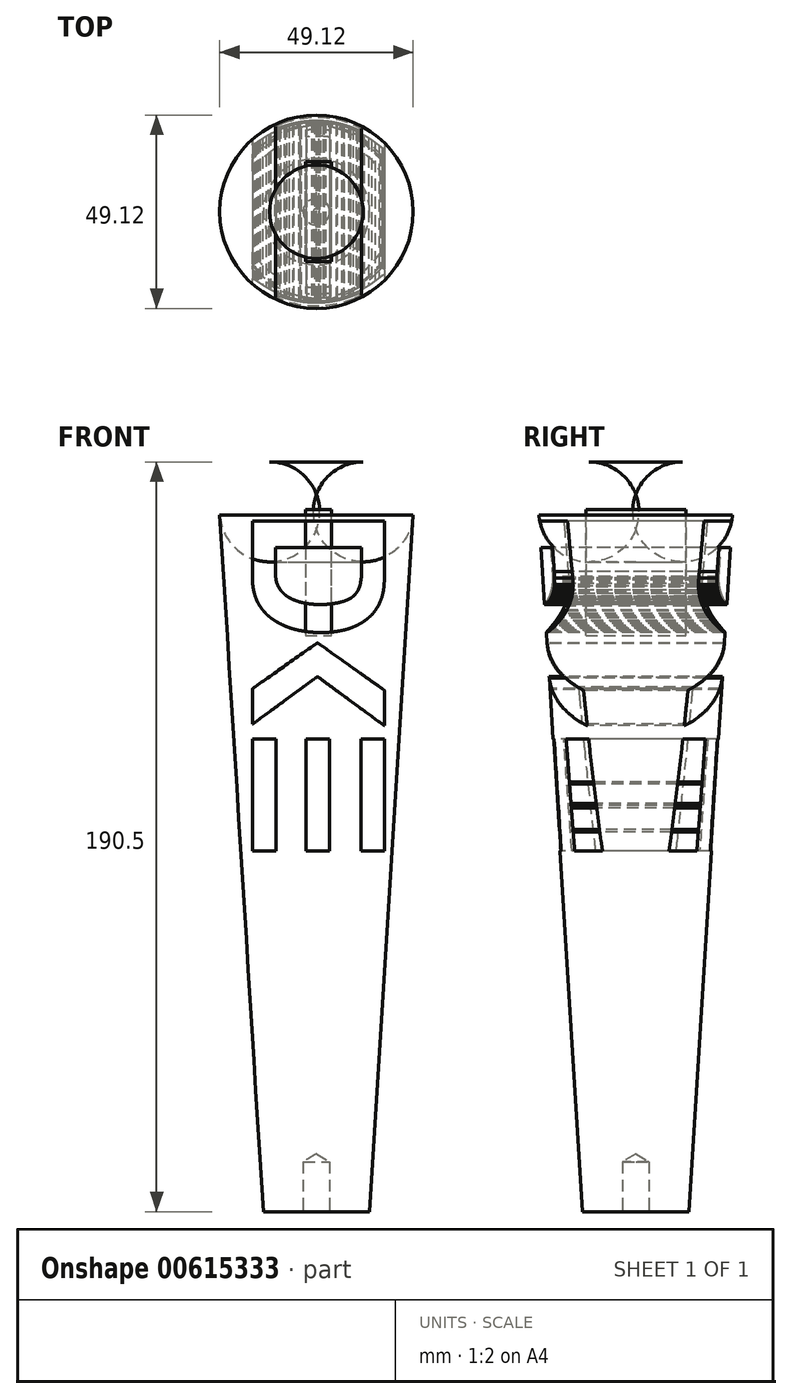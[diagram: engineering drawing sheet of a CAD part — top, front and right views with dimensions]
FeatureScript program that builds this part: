
annotation { "Feature Type Name" : "Feature", "Feature Type Description" : "" }
export const myFeature = defineFeature(function(context is Context, id is Id, definition is map)
    precondition{}
    {
        {
            var Q0;
            Q0=qCreatedBy(makeId("Front.planeOp"),FACE);
            var sketch = newSketch(context, id + "F0", { "sketchPlane" : qUnion([Q0])});
            skLineSegment(sketch, "E0", {"start": v(0, 0) * mm, "end": v(12.7, 0) * mm});
            skLineSegment(sketch, "E1", {"start": v(12.7, 0) * mm, "end": v(25.4, 203.2) * mm});
            skLineSegment(sketch, "E2", {"start": v(25.4, 203.2) * mm, "end": v(0, 203.2) * mm});
            skLineSegment(sketch, "E3", {"start": v(0, 203.2) * mm, "end": v(0, 0) * mm});
            skSolve(sketch);
        }
        {
            var Q0;
            Q0 = qSketchRegion(id + "F0", true);
            var Q1;
            Q1=sQuery(id+"F0.wireOp",EDGE,"E3");
            revolve(context, id + "F1", {"entities" : qUnion([Q0]), "axis" : qUnion([Q1]), "revolveType" : RevolveType.FULL});
        }
        {
            var Q0;
            Q0=makeQuery(id+"F1.opRevolve","SWEPT_EDGE",EDGE,{"disambiguationData":[OSD([sQuery(id+"F0.wireOp",EDGE,"E1"),sQuery(id+"F0.wireOp",EDGE,"E2")])]});
            fillet(context, id + "F2", {"entities" : qUnion([Q0]), "radius" : 12.7 * mm, "tangentPropagation" : true, "allowEdgeOverflow" : false});
        }
        {
            var Q0;
            Q0=qCreatedBy(makeId("Front.planeOp"),FACE);
            var sketch = newSketch(context, id + "F3", { "sketchPlane" : qUnion([Q0])});
            skLineSegment(sketch, "E4", {"start": v(17.27, 188.2) * mm, "end": v(17.27, 186.96) * mm});
            skLineSegment(sketch, "E5", {"start": v(17.27, 186.96) * mm, "end": v(17.27, 174.62) * mm});
            skLineSegment(sketch, "E6", {"start": v(17.27, 174.62) * mm, "end": v(17.27, 173.38) * mm});
            skLineSegment(sketch, "E7", {"start": v(17.27, 173.38) * mm, "end": v(17.26, 173.23) * mm});
            skLineSegment(sketch, "E8", {"start": v(17.26, 173.23) * mm, "end": v(17.17, 171.7) * mm});
            skLineSegment(sketch, "E9", {"start": v(17.17, 171.7) * mm, "end": v(17.16, 171.54) * mm});
            skLineSegment(sketch, "E10", {"start": v(17.16, 171.54) * mm, "end": v(17.14, 171.46) * mm});
            skLineSegment(sketch, "E11", {"start": v(17.14, 171.46) * mm, "end": v(17.04, 170.67) * mm});
            skLineSegment(sketch, "E12", {"start": v(17.04, 170.67) * mm, "end": v(17.02, 170.6) * mm});
            skLineSegment(sketch, "E13", {"start": v(17.02, 170.6) * mm, "end": v(16.96, 170.12) * mm});
            skLineSegment(sketch, "E14", {"start": v(16.96, 170.12) * mm, "end": v(16.6, 168.72) * mm});
            skLineSegment(sketch, "E15", {"start": v(16.6, 168.72) * mm, "end": v(15.88, 166.95) * mm});
            skLineSegment(sketch, "E16", {"start": v(15.88, 166.95) * mm, "end": v(14.87, 165.32) * mm});
            skLineSegment(sketch, "E17", {"start": v(14.87, 165.32) * mm, "end": v(13.94, 164.22) * mm});
            skLineSegment(sketch, "E18", {"start": v(13.94, 164.22) * mm, "end": v(13.59, 163.9) * mm});
            skLineSegment(sketch, "E19", {"start": v(13.59, 163.9) * mm, "end": v(13.22, 163.56) * mm});
            skLineSegment(sketch, "E20", {"start": v(13.22, 163.56) * mm, "end": v(12.03, 162.66) * mm});
            skLineSegment(sketch, "E21", {"start": v(12.03, 162.66) * mm, "end": v(10.3, 161.66) * mm});
            skLineSegment(sketch, "E22", {"start": v(10.3, 161.66) * mm, "end": v(8.47, 160.9) * mm});
            skLineSegment(sketch, "E23", {"start": v(8.47, 160.9) * mm, "end": v(7.04, 160.48) * mm});
            skLineSegment(sketch, "E24", {"start": v(7.04, 160.48) * mm, "end": v(6.55, 160.39) * mm});
            skLineSegment(sketch, "E25", {"start": v(6.55, 160.39) * mm, "end": v(6.42, 160.36) * mm});
            skLineSegment(sketch, "E26", {"start": v(6.42, 160.36) * mm, "end": v(5.1, 160.12) * mm});
            skLineSegment(sketch, "E27", {"start": v(5.1, 160.12) * mm, "end": v(4.96, 160.1) * mm});
            skLineSegment(sketch, "E28", {"start": v(4.96, 160.1) * mm, "end": v(4.68, 160.06) * mm});
            skLineSegment(sketch, "E29", {"start": v(4.68, 160.06) * mm, "end": v(3.29, 159.9) * mm});
            skLineSegment(sketch, "E30", {"start": v(3.29, 159.9) * mm, "end": v(1.89, 159.83) * mm});
            skLineSegment(sketch, "E31", {"start": v(1.89, 159.83) * mm, "end": v(1.6, 159.83) * mm});
            skLineSegment(sketch, "E32", {"start": v(1.6, 159.83) * mm, "end": v(1.09, 159.82) * mm});
            skLineSegment(sketch, "E33", {"start": v(1.09, 159.82) * mm, "end": v(-0.47, 159.87) * mm});
            skLineSegment(sketch, "E34", {"start": v(-0.47, 159.87) * mm, "end": v(-2.55, 160.06) * mm});
            skLineSegment(sketch, "E35", {"start": v(-2.55, 160.06) * mm, "end": v(-4.6, 160.43) * mm});
            skLineSegment(sketch, "E36", {"start": v(-4.6, 160.43) * mm, "end": v(-6.11, 160.82) * mm});
            skLineSegment(sketch, "E37", {"start": v(-6.11, 160.82) * mm, "end": v(-6.6, 160.98) * mm});
            skLineSegment(sketch, "E38", {"start": v(-6.6, 160.98) * mm, "end": v(-6.96, 161.1) * mm});
            skLineSegment(sketch, "E39", {"start": v(-6.96, 161.1) * mm, "end": v(-8.03, 161.52) * mm});
            skLineSegment(sketch, "E40", {"start": v(-8.03, 161.52) * mm, "end": v(-9.4, 162.16) * mm});
            skLineSegment(sketch, "E41", {"start": v(-9.4, 162.16) * mm, "end": v(-10.71, 162.93) * mm});
            skLineSegment(sketch, "E42", {"start": v(-10.71, 162.93) * mm, "end": v(-11.65, 163.6) * mm});
            skLineSegment(sketch, "E43", {"start": v(-11.65, 163.6) * mm, "end": v(-11.94, 163.83) * mm});
            skLineSegment(sketch, "E44", {"start": v(-11.94, 163.83) * mm, "end": v(-12.18, 164.03) * mm});
            skLineSegment(sketch, "E45", {"start": v(-12.18, 164.03) * mm, "end": v(-12.85, 164.66) * mm});
            skLineSegment(sketch, "E46", {"start": v(-12.85, 164.66) * mm, "end": v(-13.67, 165.59) * mm});
            skLineSegment(sketch, "E47", {"start": v(-13.67, 165.59) * mm, "end": v(-14.4, 166.6) * mm});
            skLineSegment(sketch, "E48", {"start": v(-14.4, 166.6) * mm, "end": v(-14.86, 167.4) * mm});
            skLineSegment(sketch, "E49", {"start": v(-14.86, 167.4) * mm, "end": v(-15, 167.67) * mm});
            skLineSegment(sketch, "E50", {"start": v(-15, 167.67) * mm, "end": v(-15.17, 168.03) * mm});
            skLineSegment(sketch, "E51", {"start": v(-15.17, 168.03) * mm, "end": v(-15.59, 169.14) * mm});
            skLineSegment(sketch, "E52", {"start": v(-15.59, 169.14) * mm, "end": v(-15.99, 170.67) * mm});
            skLineSegment(sketch, "E53", {"start": v(-15.99, 170.67) * mm, "end": v(-16.21, 172.23) * mm});
            skLineSegment(sketch, "E54", {"start": v(-16.21, 172.23) * mm, "end": v(-16.27, 173.42) * mm});
            skLineSegment(sketch, "E55", {"start": v(-16.27, 173.42) * mm, "end": v(-16.26, 173.81) * mm});
            skLineSegment(sketch, "E56", {"start": v(-16.26, 173.81) * mm, "end": v(-16.26, 175.01) * mm});
            skLineSegment(sketch, "E57", {"start": v(-16.26, 175.01) * mm, "end": v(-16.26, 187) * mm});
            skLineSegment(sketch, "E58", {"start": v(-16.26, 187) * mm, "end": v(-16.26, 188.2) * mm});
            skLineSegment(sketch, "E59", {"start": v(-16.26, 188.2) * mm, "end": v(-13.47, 188.2) * mm});
            skLineSegment(sketch, "E60", {"start": v(-13.47, 188.2) * mm, "end": v(14.47, 188.2) * mm});
            skLineSegment(sketch, "E61", {"start": v(14.47, 188.2) * mm, "end": v(17.27, 188.2) * mm});
            skLineSegment(sketch, "E62", {"start": v(16.1, 146) * mm, "end": v(16.19, 145.93) * mm});
            skLineSegment(sketch, "E63", {"start": v(16.19, 145.93) * mm, "end": v(16.69, 145.6) * mm});
            skLineSegment(sketch, "E64", {"start": v(16.69, 145.6) * mm, "end": v(17.17, 145.23) * mm});
            skLineSegment(sketch, "E65", {"start": v(17.17, 145.23) * mm, "end": v(17.26, 145.14) * mm});
            skLineSegment(sketch, "E66", {"start": v(17.26, 145.14) * mm, "end": v(17.26, 144.4) * mm});
            skLineSegment(sketch, "E67", {"start": v(17.26, 144.4) * mm, "end": v(17.26, 136.92) * mm});
            skLineSegment(sketch, "E68", {"start": v(17.26, 136.92) * mm, "end": v(17.26, 136.17) * mm});
            skLineSegment(sketch, "E69", {"start": v(17.26, 136.17) * mm, "end": v(16.35, 136.83) * mm});
            skLineSegment(sketch, "E70", {"start": v(16.35, 136.83) * mm, "end": v(7.27, 143.5) * mm});
            skLineSegment(sketch, "E71", {"start": v(7.27, 143.5) * mm, "end": v(6.36, 144.16) * mm});
            skLineSegment(sketch, "E72", {"start": v(6.36, 144.16) * mm, "end": v(5.86, 144.54) * mm});
            skLineSegment(sketch, "E73", {"start": v(5.86, 144.54) * mm, "end": v(0.78, 148.27) * mm});
            skLineSegment(sketch, "E74", {"start": v(0.78, 148.27) * mm, "end": v(0.28, 148.65) * mm});
            skLineSegment(sketch, "E75", {"start": v(0.28, 148.65) * mm, "end": v(-0.1, 148.38) * mm});
            skLineSegment(sketch, "E76", {"start": v(-0.1, 148.38) * mm, "end": v(-2.03, 146.99) * mm});
            skLineSegment(sketch, "E77", {"start": v(-2.03, 146.99) * mm, "end": v(-3.93, 145.58) * mm});
            skLineSegment(sketch, "E78", {"start": v(-3.93, 145.58) * mm, "end": v(-4.32, 145.3) * mm});
            skLineSegment(sketch, "E79", {"start": v(-4.32, 145.3) * mm, "end": v(-5.31, 144.57) * mm});
            skLineSegment(sketch, "E80", {"start": v(-5.31, 144.57) * mm, "end": v(-15.26, 137.27) * mm});
            skLineSegment(sketch, "E81", {"start": v(-15.26, 137.27) * mm, "end": v(-16.26, 136.54) * mm});
            skLineSegment(sketch, "E82", {"start": v(-16.26, 136.54) * mm, "end": v(-16.26, 137.3) * mm});
            skLineSegment(sketch, "E83", {"start": v(-16.26, 137.3) * mm, "end": v(-16.26, 143.5) * mm});
            skLineSegment(sketch, "E84", {"start": v(-16.26, 143.5) * mm, "end": v(-16.26, 145.57) * mm});
            skLineSegment(sketch, "E85", {"start": v(-16.26, 145.57) * mm, "end": v(-14.91, 146.53) * mm});
            skLineSegment(sketch, "E86", {"start": v(-14.91, 146.53) * mm, "end": v(-1.4, 156.06) * mm});
            skLineSegment(sketch, "E87", {"start": v(-1.4, 156.06) * mm, "end": v(-0.06, 157.02) * mm});
            skLineSegment(sketch, "E88", {"start": v(-0.06, 157.02) * mm, "end": v(-0.03, 157.04) * mm});
            skLineSegment(sketch, "E89", {"start": v(-0.03, 157.04) * mm, "end": v(0.06, 157.1) * mm});
            skLineSegment(sketch, "E90", {"start": v(0.06, 157.1) * mm, "end": v(0.18, 157.16) * mm});
            skLineSegment(sketch, "E91", {"start": v(0.18, 157.16) * mm, "end": v(0.31, 157.17) * mm});
            skLineSegment(sketch, "E92", {"start": v(0.31, 157.17) * mm, "end": v(0.4, 157.13) * mm});
            skLineSegment(sketch, "E93", {"start": v(0.4, 157.13) * mm, "end": v(0.43, 157.11) * mm});
            skLineSegment(sketch, "E94", {"start": v(0.43, 157.11) * mm, "end": v(1.27, 156.53) * mm});
            skLineSegment(sketch, "E95", {"start": v(1.27, 156.53) * mm, "end": v(9.58, 150.62) * mm});
            skLineSegment(sketch, "E96", {"start": v(9.58, 150.62) * mm, "end": v(10.4, 150.03) * mm});
            skLineSegment(sketch, "E97", {"start": v(10.4, 150.03) * mm, "end": v(10.88, 149.7) * mm});
            skLineSegment(sketch, "E98", {"start": v(10.88, 149.7) * mm, "end": v(15.62, 146.34) * mm});
            skLineSegment(sketch, "E99", {"start": v(15.62, 146.34) * mm, "end": v(16.1, 146) * mm});
            skLineSegment(sketch, "E100", {"start": v(11.34, 132.77) * mm, "end": v(11.83, 132.77) * mm});
            skLineSegment(sketch, "E101", {"start": v(11.83, 132.77) * mm, "end": v(16.77, 132.77) * mm});
            skLineSegment(sketch, "E102", {"start": v(16.77, 132.77) * mm, "end": v(17.27, 132.77) * mm});
            skLineSegment(sketch, "E103", {"start": v(17.27, 132.77) * mm, "end": v(17.27, 130.4) * mm});
            skLineSegment(sketch, "E104", {"start": v(17.27, 130.4) * mm, "end": v(17.27, 106.73) * mm});
            skLineSegment(sketch, "E105", {"start": v(17.27, 106.73) * mm, "end": v(17.27, 104.37) * mm});
            skLineSegment(sketch, "E106", {"start": v(17.27, 104.37) * mm, "end": v(16.77, 104.37) * mm});
            skLineSegment(sketch, "E107", {"start": v(16.77, 104.37) * mm, "end": v(11.83, 104.37) * mm});
            skLineSegment(sketch, "E108", {"start": v(11.83, 104.37) * mm, "end": v(11.34, 104.37) * mm});
            skLineSegment(sketch, "E109", {"start": v(11.34, 104.37) * mm, "end": v(11.34, 104.77) * mm});
            skLineSegment(sketch, "E110", {"start": v(11.34, 104.77) * mm, "end": v(11.34, 108.79) * mm});
            skLineSegment(sketch, "E111", {"start": v(11.34, 108.79) * mm, "end": v(11.34, 109.19) * mm});
            skLineSegment(sketch, "E112", {"start": v(11.34, 109.19) * mm, "end": v(11.32, 109.75) * mm});
            skLineSegment(sketch, "E113", {"start": v(11.32, 109.75) * mm, "end": v(11.33, 115.32) * mm});
            skLineSegment(sketch, "E114", {"start": v(11.33, 115.32) * mm, "end": v(11.34, 115.88) * mm});
            skLineSegment(sketch, "E115", {"start": v(11.34, 115.88) * mm, "end": v(11.33, 116.37) * mm});
            skLineSegment(sketch, "E116", {"start": v(11.33, 116.37) * mm, "end": v(11.32, 121.32) * mm});
            skLineSegment(sketch, "E117", {"start": v(11.32, 121.32) * mm, "end": v(11.34, 121.8) * mm});
            skLineSegment(sketch, "E118", {"start": v(11.34, 121.8) * mm, "end": v(11.34, 122.72) * mm});
            skLineSegment(sketch, "E119", {"start": v(11.34, 122.72) * mm, "end": v(11.34, 131.86) * mm});
            skLineSegment(sketch, "E120", {"start": v(11.34, 131.86) * mm, "end": v(11.34, 132.77) * mm});
            skLineSegment(sketch, "E121", {"start": v(11.46, 175.86) * mm, "end": v(11.46, 175.33) * mm});
            skLineSegment(sketch, "E122", {"start": v(11.46, 175.33) * mm, "end": v(11.39, 173.74) * mm});
            skLineSegment(sketch, "E123", {"start": v(11.39, 173.74) * mm, "end": v(11.1, 172) * mm});
            skLineSegment(sketch, "E124", {"start": v(11.1, 172) * mm, "end": v(11, 171.65) * mm});
            skLineSegment(sketch, "E125", {"start": v(11, 171.65) * mm, "end": v(10.93, 171.4) * mm});
            skLineSegment(sketch, "E126", {"start": v(10.93, 171.4) * mm, "end": v(10.62, 170.68) * mm});
            skLineSegment(sketch, "E127", {"start": v(10.62, 170.68) * mm, "end": v(10.06, 169.79) * mm});
            skLineSegment(sketch, "E128", {"start": v(10.06, 169.79) * mm, "end": v(9.34, 169.03) * mm});
            skLineSegment(sketch, "E129", {"start": v(9.34, 169.03) * mm, "end": v(8.7, 168.56) * mm});
            skLineSegment(sketch, "E130", {"start": v(8.7, 168.56) * mm, "end": v(8.47, 168.44) * mm});
            skLineSegment(sketch, "E131", {"start": v(8.47, 168.44) * mm, "end": v(8.1, 168.25) * mm});
            skLineSegment(sketch, "E132", {"start": v(8.1, 168.25) * mm, "end": v(6.92, 167.78) * mm});
            skLineSegment(sketch, "E133", {"start": v(6.92, 167.78) * mm, "end": v(5.28, 167.35) * mm});
            skLineSegment(sketch, "E134", {"start": v(5.28, 167.35) * mm, "end": v(3.6, 167.1) * mm});
            skLineSegment(sketch, "E135", {"start": v(3.6, 167.1) * mm, "end": v(2.35, 167) * mm});
            skLineSegment(sketch, "E136", {"start": v(2.35, 167) * mm, "end": v(1.92, 166.97) * mm});
            skLineSegment(sketch, "E137", {"start": v(1.92, 166.97) * mm, "end": v(1.7, 166.98) * mm});
            skLineSegment(sketch, "E138", {"start": v(1.7, 166.98) * mm, "end": v(0.53, 166.97) * mm});
            skLineSegment(sketch, "E139", {"start": v(0.53, 166.97) * mm, "end": v(-0.63, 167) * mm});
            skLineSegment(sketch, "E140", {"start": v(-0.63, 167) * mm, "end": v(-0.87, 167.03) * mm});
            skLineSegment(sketch, "E141", {"start": v(-0.87, 167.03) * mm, "end": v(-1.3, 167.06) * mm});
            skLineSegment(sketch, "E142", {"start": v(-1.3, 167.06) * mm, "end": v(-2.56, 167.23) * mm});
            skLineSegment(sketch, "E143", {"start": v(-2.56, 167.23) * mm, "end": v(-4.24, 167.6) * mm});
            skLineSegment(sketch, "E144", {"start": v(-4.24, 167.6) * mm, "end": v(-5.85, 168.16) * mm});
            skLineSegment(sketch, "E145", {"start": v(-5.85, 168.16) * mm, "end": v(-7, 168.74) * mm});
            skLineSegment(sketch, "E146", {"start": v(-7, 168.74) * mm, "end": v(-7.35, 168.97) * mm});
            skLineSegment(sketch, "E147", {"start": v(-7.35, 168.97) * mm, "end": v(-7.6, 169.13) * mm});
            skLineSegment(sketch, "E148", {"start": v(-7.6, 169.13) * mm, "end": v(-8.3, 169.7) * mm});
            skLineSegment(sketch, "E149", {"start": v(-8.3, 169.7) * mm, "end": v(-9.1, 170.6) * mm});
            skLineSegment(sketch, "E150", {"start": v(-9.1, 170.6) * mm, "end": v(-9.73, 171.61) * mm});
            skLineSegment(sketch, "E151", {"start": v(-9.73, 171.61) * mm, "end": v(-10.08, 172.44) * mm});
            skLineSegment(sketch, "E152", {"start": v(-10.08, 172.44) * mm, "end": v(-10.15, 172.73) * mm});
            skLineSegment(sketch, "E153", {"start": v(-10.15, 172.73) * mm, "end": v(-10.22, 172.96) * mm});
            skLineSegment(sketch, "E154", {"start": v(-10.22, 172.96) * mm, "end": v(-10.4, 174.13) * mm});
            skLineSegment(sketch, "E155", {"start": v(-10.4, 174.13) * mm, "end": v(-10.44, 175.3) * mm});
            skLineSegment(sketch, "E156", {"start": v(-10.44, 175.3) * mm, "end": v(-10.44, 175.54) * mm});
            skLineSegment(sketch, "E157", {"start": v(-10.44, 175.54) * mm, "end": v(-10.44, 176.03) * mm});
            skLineSegment(sketch, "E158", {"start": v(-10.44, 176.03) * mm, "end": v(-10.44, 180.91) * mm});
            skLineSegment(sketch, "E159", {"start": v(-10.44, 180.91) * mm, "end": v(-10.44, 181.4) * mm});
            skLineSegment(sketch, "E160", {"start": v(-10.44, 181.4) * mm, "end": v(-8.62, 181.4) * mm});
            skLineSegment(sketch, "E161", {"start": v(-8.62, 181.4) * mm, "end": v(9.63, 181.4) * mm});
            skLineSegment(sketch, "E162", {"start": v(9.63, 181.4) * mm, "end": v(11.46, 181.4) * mm});
            skLineSegment(sketch, "E163", {"start": v(11.46, 181.4) * mm, "end": v(11.46, 180.01) * mm});
            skLineSegment(sketch, "E164", {"start": v(11.46, 180.01) * mm, "end": v(11.46, 176.32) * mm});
            skLineSegment(sketch, "E165", {"start": v(11.46, 176.32) * mm, "end": v(11.46, 175.86) * mm});
            skLineSegment(sketch, "E166", {"start": v(3.29, 132.77) * mm, "end": v(3.29, 130.4) * mm});
            skLineSegment(sketch, "E167", {"start": v(3.29, 130.4) * mm, "end": v(3.29, 106.73) * mm});
            skLineSegment(sketch, "E168", {"start": v(3.29, 106.73) * mm, "end": v(3.29, 104.37) * mm});
            skLineSegment(sketch, "E169", {"start": v(3.29, 104.37) * mm, "end": v(2.8, 104.37) * mm});
            skLineSegment(sketch, "E170", {"start": v(2.8, 104.37) * mm, "end": v(-2.16, 104.37) * mm});
            skLineSegment(sketch, "E171", {"start": v(-2.16, 104.37) * mm, "end": v(-2.65, 104.37) * mm});
            skLineSegment(sketch, "E172", {"start": v(-2.65, 104.37) * mm, "end": v(-2.66, 106.74) * mm});
            skLineSegment(sketch, "E173", {"start": v(-2.66, 106.74) * mm, "end": v(-2.65, 130.4) * mm});
            skLineSegment(sketch, "E174", {"start": v(-2.65, 130.4) * mm, "end": v(-2.65, 132.76) * mm});
            skLineSegment(sketch, "E175", {"start": v(-2.65, 132.76) * mm, "end": v(-2.15, 132.77) * mm});
            skLineSegment(sketch, "E176", {"start": v(-2.15, 132.77) * mm, "end": v(2.8, 132.77) * mm});
            skLineSegment(sketch, "E177", {"start": v(2.8, 132.77) * mm, "end": v(3.29, 132.77) * mm});
            skLineSegment(sketch, "E178", {"start": v(-10.3, 132.77) * mm, "end": v(-10.3, 130.4) * mm});
            skLineSegment(sketch, "E179", {"start": v(-10.3, 130.4) * mm, "end": v(-10.3, 106.73) * mm});
            skLineSegment(sketch, "E180", {"start": v(-10.3, 106.73) * mm, "end": v(-10.3, 104.37) * mm});
            skLineSegment(sketch, "E181", {"start": v(-10.3, 104.37) * mm, "end": v(-10.8, 104.37) * mm});
            skLineSegment(sketch, "E182", {"start": v(-10.8, 104.37) * mm, "end": v(-15.75, 104.37) * mm});
            skLineSegment(sketch, "E183", {"start": v(-15.75, 104.37) * mm, "end": v(-16.25, 104.37) * mm});
            skLineSegment(sketch, "E184", {"start": v(-16.25, 104.37) * mm, "end": v(-16.25, 106.74) * mm});
            skLineSegment(sketch, "E185", {"start": v(-16.25, 106.74) * mm, "end": v(-16.25, 130.4) * mm});
            skLineSegment(sketch, "E186", {"start": v(-16.25, 130.4) * mm, "end": v(-16.25, 132.77) * mm});
            skLineSegment(sketch, "E187", {"start": v(-16.25, 132.77) * mm, "end": v(-15.75, 132.77) * mm});
            skLineSegment(sketch, "E188", {"start": v(-15.75, 132.77) * mm, "end": v(-10.8, 132.77) * mm});
            skLineSegment(sketch, "E189", {"start": v(-10.8, 132.77) * mm, "end": v(-10.3, 132.77) * mm});
            skSolve(sketch);
        }
        {
            var Q0;
            Q0 = qSketchRegion(id + "F3", true);
            extrude(context, id + "F4", {"entities" : qUnion([Q0]), "operationType" : NewBodyOperationType.REMOVE, "endBound" : BoundingType.THROUGH_ALL, "oppositeDirection" : true, "depth" : 25.4 * mm, "offsetDistance" : 25.4 * mm, "hasSecondDirection" : true, "secondDirectionBound" : SecondDirectionBoundingType.THROUGH_ALL, "secondDirectionOppositeDirection" : false, "secondDirectionDepth" : 25.4 * mm});
        }
        {
            var Q0;
            Q0=qCreatedBy(makeId("Front.planeOp"),FACE);
            var sketch = newSketch(context, id + "F5", { "sketchPlane" : qUnion([Q0])});
            skLineSegment(sketch, "E190", {"start": v(0, 191.05) * mm, "end": v(-2.82, 191.05) * mm});
            skLineSegment(sketch, "E191", {"start": v(-2.82, 191.05) * mm, "end": v(-2.82, 159.08) * mm});
            skLineSegment(sketch, "E192", {"start": v(-2.82, 159.08) * mm, "end": v(3.84, 159.08) * mm});
            skLineSegment(sketch, "E193", {"start": v(3.84, 159.08) * mm, "end": v(3.84, 191.13) * mm});
            skLineSegment(sketch, "E194", {"start": v(3.84, 191.13) * mm, "end": v(0, 191.05) * mm});
            skSolve(sketch);
        }
        {
            var Q0;
            Q0 = qSketchRegion(id + "F5", true);
            extrude(context, id + "F6", {"entities" : qUnion([Q0]), "depth" : 12.7 * mm, "offsetDistance" : 25.4 * mm, "hasSecondDirection" : true, "secondDirectionOppositeDirection" : true, "secondDirectionDepth" : 12.7 * mm});
        }
        {
            var Q0;
            Q0=makeQuery(id+"F1.opRevolve","SWEPT_FACE",FACE,{"disambiguationData":[OSD([sQuery(id+"F0.wireOp",EDGE,"E0")])]});
            var sketch = newSketch(context, id + "F7", { "sketchPlane" : qUnion([Q0])});
            skPoint(sketch, "E195", {"position": v(0, 0) * mm});
            skSolve(sketch);
        }
        {
            var Q0;
            Q0=sQuery(id+"F7.wireOp",VERTEX,"E195");
            var Q1;
            Q1=makeQuery(id+"F4.boolean.opBoolean","SPLIT",BODY,{"disambiguationData":[OD(0.0)],"derivedFrom":makeQuery(id+"F1.opRevolve","SWEPT_BODY",BODY,{"disambiguationData":[OSD([sQuery(id+"F0.wireOp",EDGE,"E0"),sQuery(id+"F0.wireOp",EDGE,"E1"),sQuery(id+"F0.wireOp",EDGE,"E2"),sQuery(id+"F0.wireOp",EDGE,"E3")])]})});
            hole(context, id + "F8", {"style" : HoleStyle.SIMPLE, "endStyle" : HoleEndStyle.BLIND, "standardTappedOrClearance" : lookupTablePath({ "standard" : "ANSI", "fit" : "Normal (ASME)", "size" : "1/4", "type" : "Clearance" }), "standardBlindInLast" : lookupTablePath({ "fit" : "Free", "standard" : "ANSI", "size" : "1/4", "type" : "Clearance" }), "holeDiameter" : 6.76 * mm, "majorDiameter" : 6.35 * mm, "holeDepth" : 25.4 * mm, "isTappedThrough" : true, "tappedDepth" : 12.7 * mm, "tapClearance" : 3, "locations" : qUnion([Q0]), "scope" : qUnion([Q1])});
        }
        {
            var Q0;
            Q0=qCreatedBy(makeId("Front.planeOp"),FACE);
            var sketch = newSketch(context, id + "F9", { "sketchPlane" : qUnion([Q0])});
            skLineSegment(sketch, "E196.bottom", {"start": v(-39.59, 0) * mm, "end": v(44.1, 0) * mm});
            skLineSegment(sketch, "E196.top", {"start": v(-39.59, 12.7) * mm, "end": v(44.1, 12.7) * mm});
            skLineSegment(sketch, "E196.left", {"start": v(-39.59, 0) * mm, "end": v(-39.59, 12.7) * mm});
            skLineSegment(sketch, "E196.right", {"start": v(44.1, 0) * mm, "end": v(44.1, 12.7) * mm});
            skSolve(sketch);
        }
        {
            var Q0;
            Q0=makeQuery(id+"F9.imprint","IMPRINT",FACE,{"disambiguationData":[TD([[makeQuery(id+"F9.imprint","IMPRINT",EDGE,{"derivedFrom":sQuery(id+"F9.wireOp",EDGE,"E196.bottom")}),1.0]])]});
            extrude(context, id + "F10", {"entities" : qUnion([Q0]), "operationType" : NewBodyOperationType.REMOVE, "endBound" : BoundingType.THROUGH_ALL, "oppositeDirection" : true, "depth" : 25.4 * mm, "offsetDistance" : 25.4 * mm, "hasSecondDirection" : true, "secondDirectionBound" : SecondDirectionBoundingType.THROUGH_ALL, "secondDirectionOppositeDirection" : false, "secondDirectionDepth" : 25.4 * mm});
        }
    });
